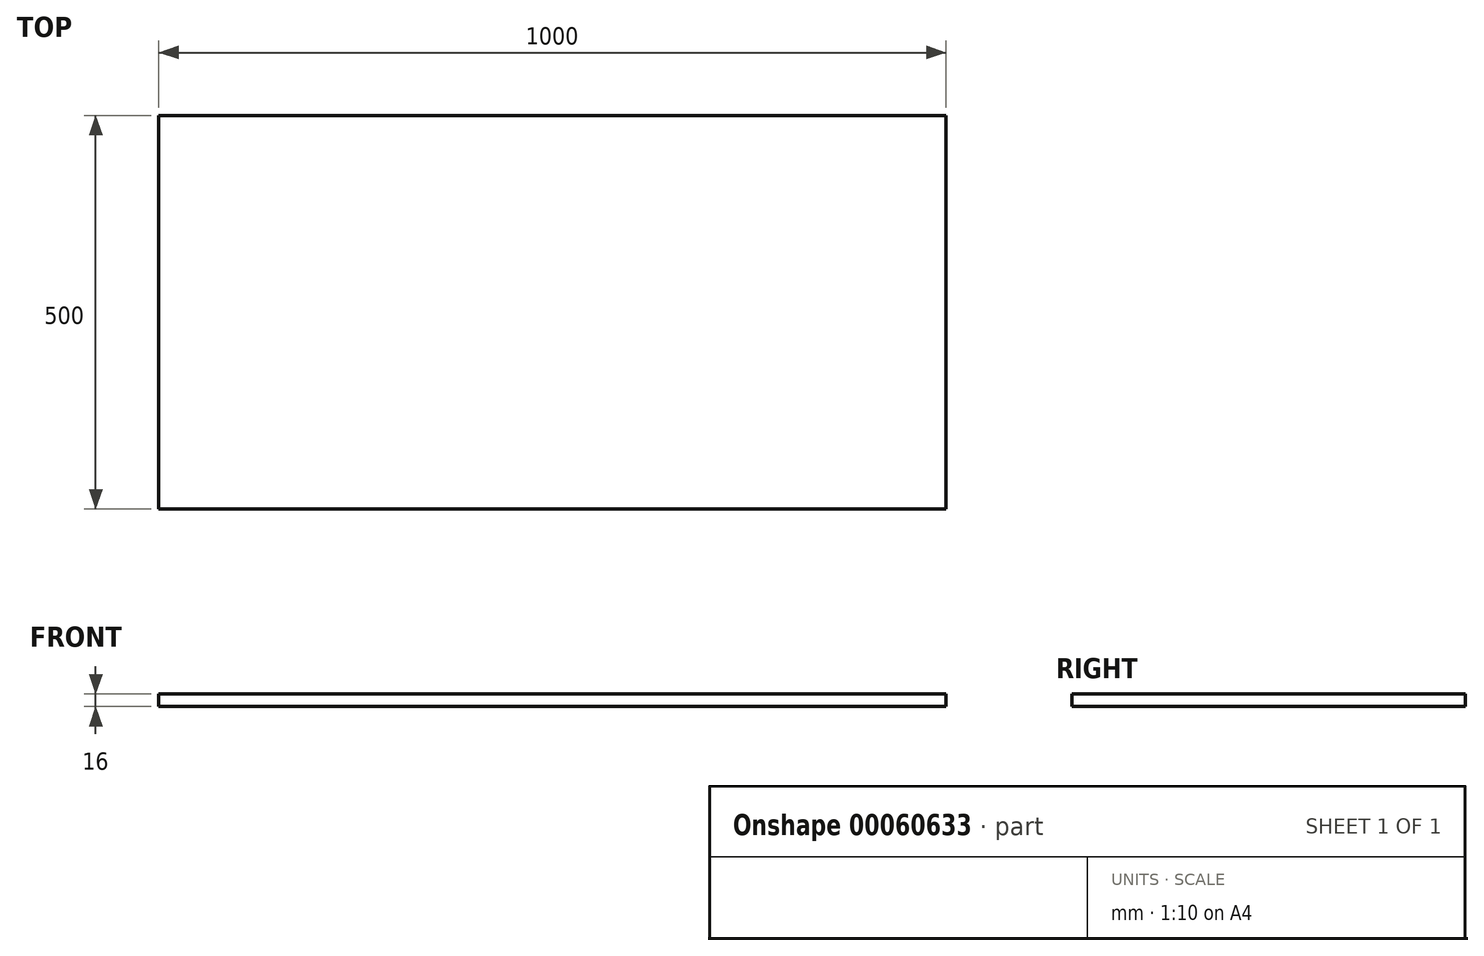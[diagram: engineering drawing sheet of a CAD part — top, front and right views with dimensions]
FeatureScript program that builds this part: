
annotation { "Feature Type Name" : "Feature", "Feature Type Description" : "" }
export const myFeature = defineFeature(function(context is Context, id is Id, definition is map)
    precondition{}
    {
        {
            var Q0;
            Q0=qCreatedBy(makeId("Top.planeOp"),FACE);
            var sketch = newSketch(context, id + "F0", { "sketchPlane" : qUnion([Q0])});
            skLineSegment(sketch, "E0.bottom", {"start": v(0, 0) * mm, "end": v(1000, 0) * mm});
            skLineSegment(sketch, "E0.top", {"start": v(0, -500) * mm, "end": v(1000, -500) * mm});
            skLineSegment(sketch, "E0.left", {"start": v(0, 0) * mm, "end": v(0, -500) * mm});
            skLineSegment(sketch, "E0.right", {"start": v(1000, 0) * mm, "end": v(1000, -500) * mm});
            skSolve(sketch);
        }
        {
            var Q0;
            Q0 = qSketchRegion(id + "F0", true);
            extrude(context, id + "F1", {"entities" : qUnion([Q0]), "depth" : 16 * mm});
        }
    });
